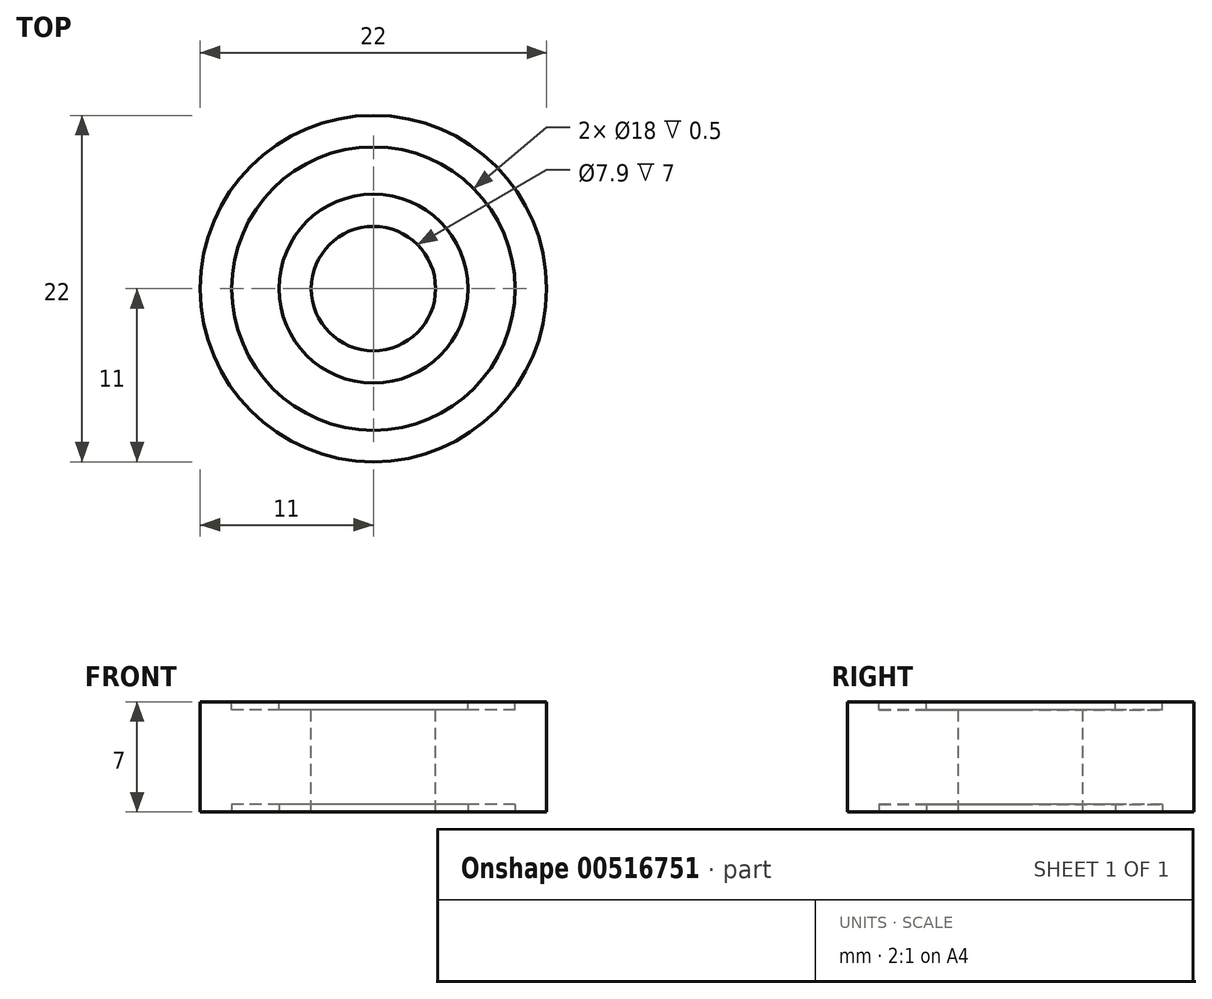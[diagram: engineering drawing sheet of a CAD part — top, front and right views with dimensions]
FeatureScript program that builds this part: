
annotation { "Feature Type Name" : "Feature", "Feature Type Description" : "" }
export const myFeature = defineFeature(function(context is Context, id is Id, definition is map)
    precondition{}
    {
        {
            var Q0;
            Q0=qCreatedBy(makeId("Top.planeOp"),FACE);
            var sketch = newSketch(context, id + "F0", { "sketchPlane" : qUnion([Q0])});
            skCircle(sketch, "E0", {"center": v(0, 0) * mm, "radius": 11 * mm});
            skSolve(sketch);
        }
        {
            var Q0;
            Q0=makeQuery(id+"F0.imprint","IMPRINT",FACE,{"disambiguationData":[TD([[makeQuery(id+"F0.imprint","IMPRINT",EDGE,{"derivedFrom":sQuery(id+"F0.wireOp",EDGE,"E0")}),1.0]])]});
            extrude(context, id + "F1", {"entities" : qUnion([Q0]), "depth" : 7 * mm, "offsetDistance" : 25 * mm});
        }
        {
            var Q0;
            Q0=makeQuery(id+"F1.opExtrude","CAP_FACE",FACE,{"disambiguationData":[OSD([sQuery(id+"F0.wireOp",EDGE,"E0")])],"isStart":false});
            var sketch = newSketch(context, id + "F2", { "sketchPlane" : qUnion([Q0])});
            skCircle(sketch, "E1", {"center": v(0, 0) * mm, "radius": 9 * mm});
            skCircle(sketch, "E2", {"center": v(0, 0) * mm, "radius": 6 * mm});
            skSolve(sketch);
        }
        {
            var Q0;
            Q0=makeQuery(id+"F2.imprint","IMPRINT",FACE,{"disambiguationData":[TD([[makeQuery(id+"F2.imprint","IMPRINT",EDGE,{"derivedFrom":sQuery(id+"F2.wireOp",EDGE,"E1")}),1.0]])]});
            extrude(context, id + "F3", {"entities" : qUnion([Q0]), "operationType" : NewBodyOperationType.REMOVE, "oppositeDirection" : true, "depth" : 0.5 * mm, "offsetDistance" : 25 * mm});
        }
        {
            var Q0;
            Q0=makeQuery(id+"F3.boolean.opBoolean","SPLIT",FACE,{"disambiguationData":[TD([makeQuery(id+"F3.opExtrude","SWEPT_FACE",FACE,{"disambiguationData":[OSD([sQuery(id+"F2.wireOp",EDGE,"E2")])]})])],"derivedFrom":makeQuery(id+"F1.opExtrude","CAP_FACE",FACE,{"disambiguationData":[OSD([sQuery(id+"F0.wireOp",EDGE,"E0")])],"isStart":false})});
            var sketch = newSketch(context, id + "F4", { "sketchPlane" : qUnion([Q0])});
            skCircle(sketch, "E3", {"center": v(0, 0) * mm, "radius": 3.95 * mm});
            skSolve(sketch);
        }
        {
            var Q0;
            Q0=makeQuery(id+"F4.imprint","IMPRINT",FACE,{"disambiguationData":[TD([[makeQuery(id+"F4.imprint","IMPRINT",EDGE,{"derivedFrom":sQuery(id+"F4.wireOp",EDGE,"E3")}),1.0]])]});
            extrude(context, id + "F5", {"entities" : qUnion([Q0]), "operationType" : NewBodyOperationType.REMOVE, "endBound" : BoundingType.THROUGH_ALL, "oppositeDirection" : true, "depth" : 25 * mm, "offsetDistance" : 25 * mm});
        }
        {
            var Q0;
            Q0=makeQuery(id+"F0.imprint","IMPRINT",FACE,{"disambiguationData":[TD([[makeQuery(id+"F0.imprint","IMPRINT",EDGE,{"derivedFrom":sQuery(id+"F0.wireOp",EDGE,"E0")}),1.0]])]});
            var sketch = newSketch(context, id + "F6", { "sketchPlane" : qUnion([Q0])});
            skCircle(sketch, "E4", {"center": v(0, 0) * mm, "radius": 9 * mm});
            skCircle(sketch, "E5", {"center": v(0, 0) * mm, "radius": 6 * mm});
            skSolve(sketch);
        }
        {
            var Q0;
            Q0=makeQuery(id+"F6.imprint","IMPRINT",FACE,{"disambiguationData":[TD([[makeQuery(id+"F6.imprint","IMPRINT",EDGE,{"derivedFrom":sQuery(id+"F6.wireOp",EDGE,"E4")}),1.0]])]});
            extrude(context, id + "F7", {"entities" : qUnion([Q0]), "operationType" : NewBodyOperationType.REMOVE, "depth" : 0.5 * mm, "offsetDistance" : 25 * mm});
        }
    });
